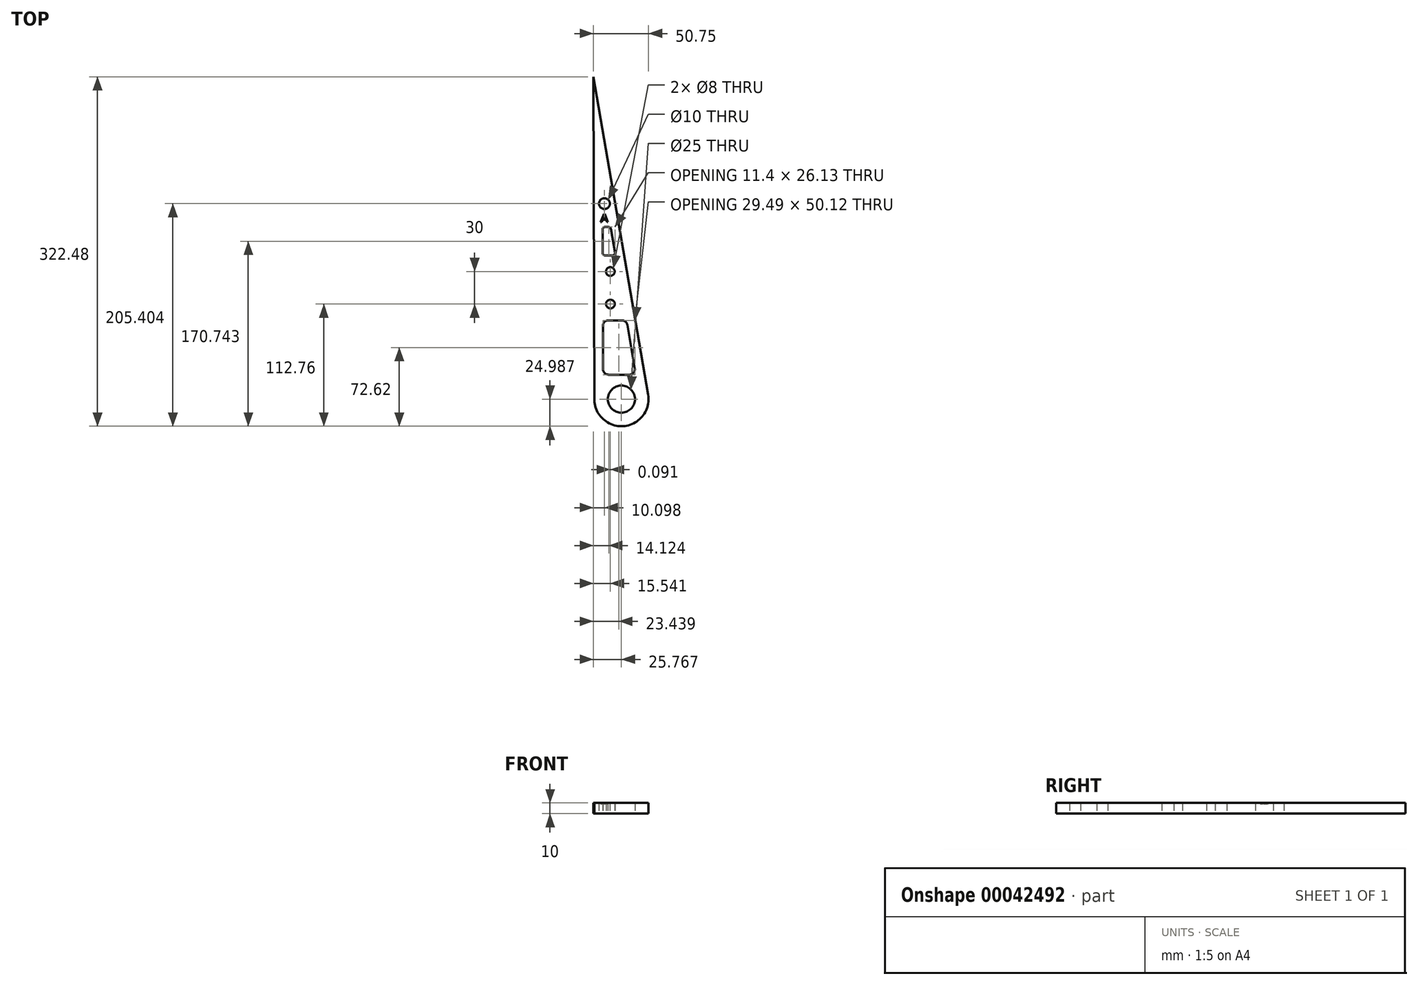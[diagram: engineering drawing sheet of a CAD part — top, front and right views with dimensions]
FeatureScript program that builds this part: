
annotation { "Feature Type Name" : "Feature", "Feature Type Description" : "" }
export const myFeature = defineFeature(function(context is Context, id is Id, definition is map)
    precondition{}
    {
        {
            var Q0;
            Q0=qCreatedBy(makeId("Top.planeOp"),FACE);
            var sketch = newSketch(context, id + "F0", { "sketchPlane" : qUnion([Q0])});
            skLineSegment(sketch, "E0", {"start": v(-19.63, -57.7) * mm, "end": v(-20.54, 242.3) * mm});
            skArc(sketch, "E1", {"start": v(-19.63, -57.7) * mm, "mid": v(8.6, -79.95) * mm, "end": v(29.85, -50.96) * mm});
            skPoint(sketch, "E1.second.point", {"position": v(-6.38, -77.32) * mm});
            skPoint(sketch, "E1.third.point", {"position": v(23.08, -37.7) * mm});
            skLineSegment(sketch, "E2", {"start": v(-20.54, 242.3) * mm, "end": v(29.85, -50.96) * mm});
            skCircle(sketch, "E3", {"center": v(5.23, -55.2) * mm, "radius": 12.5 * mm});
            skLineSegment(sketch, "E4", {"start": v(-10.05, 77.5) * mm, "end": v(-2.71, 77.5) * mm});
            skPoint(sketch, "E5.start.orphan", {"position": v(-20.09, 92.3) * mm});
            skCircle(sketch, "E6", {"center": v(-10.44, 125.22) * mm, "radius": 5 * mm});
            skLineSegment(sketch, "E7", {"start": v(-10.12, 103.63) * mm, "end": v(-6.52, 103.63) * mm});
            skLineSegment(sketch, "E8", {"start": v(-12.12, 101.62) * mm, "end": v(-12.05, 79.5) * mm});
            skLineSegment(sketch, "E9", {"start": v(-6.73, -32.62) * mm, "end": v(12.65, -32.62) * mm});
            skPoint(sketch, "E10.orphan", {"position": v(20.45, -43.47) * mm});
            skLineSegment(sketch, "E11.trimOffspring", {"start": v(10.68, 13.35) * mm, "end": v(17.58, -26.77) * mm});
            skPoint(sketch, "E12.orphan", {"position": v(4.75, 47.86) * mm});
            skLineSegment(sketch, "E13.trimOffspring", {"start": v(-11.85, 12.48) * mm, "end": v(-11.73, -27.63) * mm});
            skLineSegment(sketch, "E14.trimOffspring", {"start": v(-6.85, 17.5) * mm, "end": v(5.76, 17.5) * mm});
            skLineSegment(sketch, "E15.trimOffspring", {"start": v(-4.54, 101.96) * mm, "end": v(-0.74, 79.84) * mm});
            skPoint(sketch, "E16.orphan", {"position": v(-10.94, 139.18) * mm});
            skPoint(sketch, "E17.visualSharp", {"position": v(-11.71, -32.62) * mm});
            skArc(sketch, "E17.filletArc", {"start": v(-11.73, -27.63) * mm, "mid": v(-10.26, -31.16) * mm, "end": v(-6.73, -32.62) * mm});
            skPoint(sketch, "E18.visualSharp", {"position": v(18.58, -32.62) * mm});
            skArc(sketch, "E18.filletArc", {"start": v(12.65, -32.62) * mm, "mid": v(16.47, -30.84) * mm, "end": v(17.58, -26.77) * mm});
            skPoint(sketch, "E19.visualSharp", {"position": v(-11.86, 17.5) * mm});
            skArc(sketch, "E19.filletArc", {"start": v(-6.85, 17.5) * mm, "mid": v(-10.39, 16.03) * mm, "end": v(-11.85, 12.48) * mm});
            skPoint(sketch, "E20.visualSharp", {"position": v(9.97, 17.5) * mm});
            skArc(sketch, "E20.filletArc", {"start": v(10.68, 13.35) * mm, "mid": v(8.98, 16.32) * mm, "end": v(5.76, 17.5) * mm});
            skPoint(sketch, "E21.visualSharp", {"position": v(-4.83, 103.63) * mm});
            skArc(sketch, "E21.filletArc", {"start": v(-4.54, 101.96) * mm, "mid": v(-5.23, 103.15) * mm, "end": v(-6.52, 103.63) * mm});
            skPoint(sketch, "E22.visualSharp", {"position": v(-12.12, 103.63) * mm});
            skArc(sketch, "E22.filletArc", {"start": v(-10.12, 103.63) * mm, "mid": v(-11.53, 103.04) * mm, "end": v(-12.12, 101.62) * mm});
            skPoint(sketch, "E23.visualSharp", {"position": v(-12.04, 77.5) * mm});
            skArc(sketch, "E23.filletArc", {"start": v(-12.05, 79.5) * mm, "mid": v(-11.46, 78.08) * mm, "end": v(-10.05, 77.5) * mm});
            skPoint(sketch, "E24.visualSharp", {"position": v(-0.34, 77.5) * mm});
            skArc(sketch, "E24.filletArc", {"start": v(-2.71, 77.5) * mm, "mid": v(-1.18, 78.21) * mm, "end": v(-0.74, 79.84) * mm});
            skLineSegment(sketch, "E25", {"start": v(-5.04, 75.08) * mm, "end": v(-4.88, 22.28) * mm, "construction": true});
            skCircle(sketch, "E26", {"center": v(-5, 62.58) * mm, "radius": 4 * mm});
            skCircle(sketch, "E27", {"center": v(-4.9, 32.58) * mm, "radius": 4 * mm});
            skSolve(sketch);
        }
        {
            var Q0;
            Q0=qSketchRegion(id+"F0",true);
            extrude(context, id + "F1", {"entities" : qUnion([Q0]), "depth" : 10 * mm});
        }
        {
            var Q0;
            Q0=makeQuery(id+"F1.opExtrude","CAP_FACE",FACE,{"disambiguationData":[OSD([sQuery(id+"F0.wireOp",EDGE,"E0"),sQuery(id+"F0.wireOp",EDGE,"E1"),sQuery(id+"F0.wireOp",EDGE,"E2"),sQuery(id+"F0.wireOp",EDGE,"E3"),sQuery(id+"F0.wireOp",EDGE,"E4"),sQuery(id+"F0.wireOp",EDGE,"E6"),sQuery(id+"F0.wireOp",EDGE,"E7"),sQuery(id+"F0.wireOp",EDGE,"E8"),sQuery(id+"F0.wireOp",EDGE,"E9"),sQuery(id+"F0.wireOp",EDGE,"E11.trimOffspring"),sQuery(id+"F0.wireOp",EDGE,"E13.trimOffspring"),sQuery(id+"F0.wireOp",EDGE,"E14.trimOffspring"),sQuery(id+"F0.wireOp",EDGE,"E15.trimOffspring"),sQuery(id+"F0.wireOp",EDGE,"E17.filletArc"),sQuery(id+"F0.wireOp",EDGE,"E18.filletArc"),sQuery(id+"F0.wireOp",EDGE,"E19.filletArc"),sQuery(id+"F0.wireOp",EDGE,"E20.filletArc"),sQuery(id+"F0.wireOp",EDGE,"E21.filletArc"),sQuery(id+"F0.wireOp",EDGE,"E22.filletArc"),sQuery(id+"F0.wireOp",EDGE,"E23.filletArc"),sQuery(id+"F0.wireOp",EDGE,"E24.filletArc"),sQuery(id+"F0.wireOp",EDGE,"E26"),sQuery(id+"F0.wireOp",EDGE,"E27")])],"isStart":false});
            var sketch = newSketch(context, id + "F2", { "sketchPlane" : qUnion([Q0])});
            skText(sketch, "E28", { "text": "A", "fontName": "OpenSans-Regular.ttf"});
            const initialGuessF2  = {"E28": [-0.01387, 0.10812, 1, 0, 0.00765]};
            skSetInitialGuess(sketch, initialGuessF2);
            skSolve(sketch);
        }
        {
            var Q0;
            Q0 = qSketchRegion(id + "F2", true);
            extrude(context, id + "F3", {"entities" : qUnion([Q0]), "operationType" : NewBodyOperationType.REMOVE, "oppositeDirection" : true, "depth" : 1 * mm});
        }
    });
